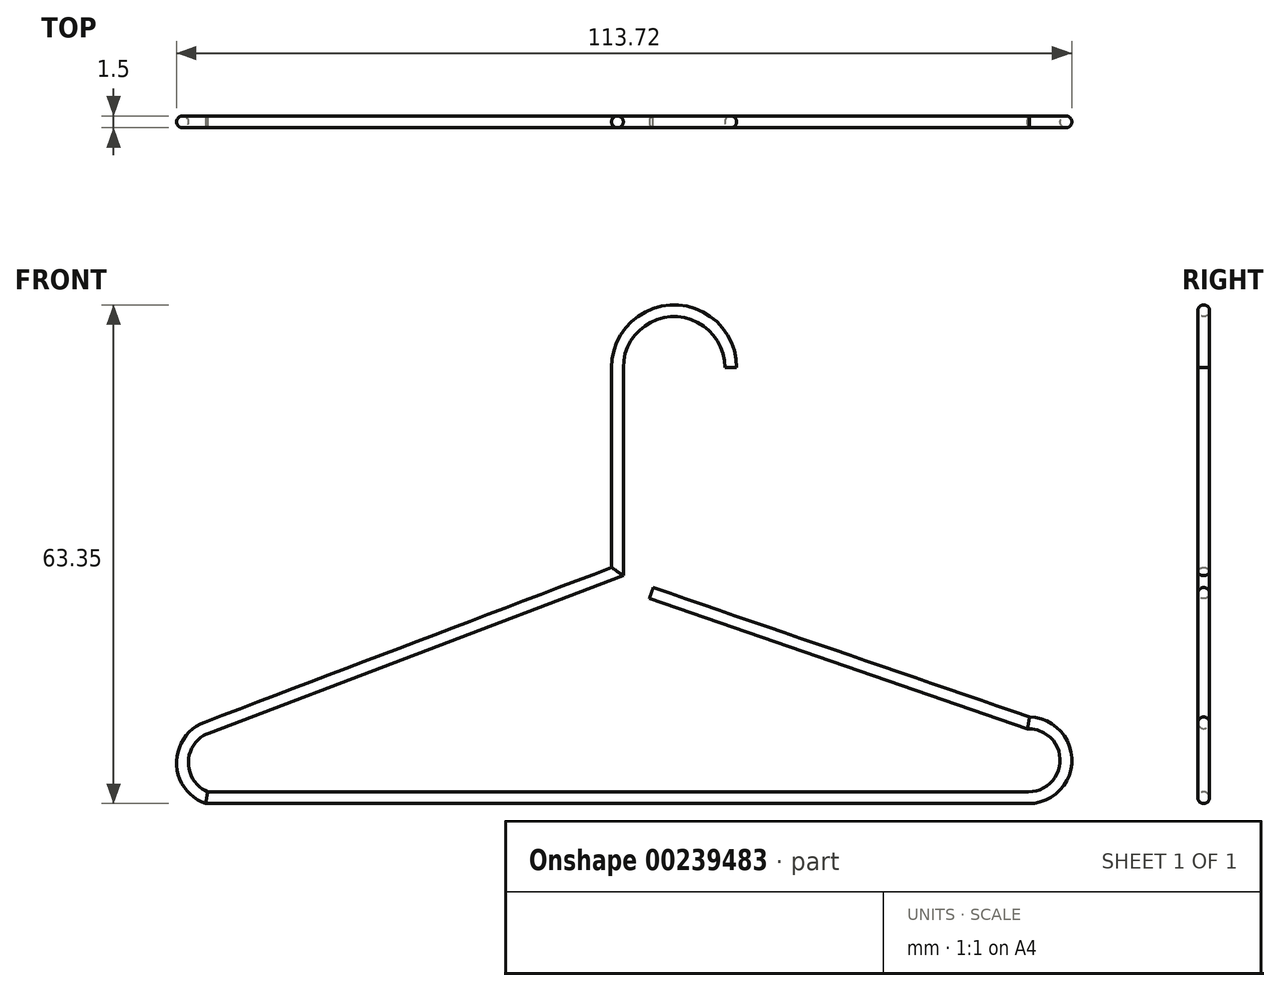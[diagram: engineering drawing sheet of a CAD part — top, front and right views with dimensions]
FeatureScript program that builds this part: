
annotation { "Feature Type Name" : "Feature", "Feature Type Description" : "" }
export const myFeature = defineFeature(function(context is Context, id is Id, definition is map)
    precondition{}
    {
        {
            var Q0;
            Q0=qCreatedBy(makeId("Front.planeOp"),FACE);
            var sketch = newSketch(context, id + "F0", { "sketchPlane" : qUnion([Q0])});
            skLineSegment(sketch, "E0", {"start": v(0, 0) * mm, "end": v(0, 25.95) * mm});
            skArc(sketch, "E1", {"start": v(14.35, 25.95) * mm, "mid": v(7.17, 33.12) * mm, "end": v(0, 25.95) * mm});
            skLineSegment(sketch, "E2", {"start": v(0, 0) * mm, "end": v(-52.2, -19.84) * mm});
            skArc(sketch, "E3", {"start": v(-52.2, -19.84) * mm, "mid": v(-55.25, -24.27) * mm, "end": v(-52.2, -28.7) * mm});
            skLineSegment(sketch, "E4", {"start": v(-52.2, -28.7) * mm, "end": v(52.2, -28.7) * mm});
            skArc(sketch, "E5", {"start": v(52.2, -28.7) * mm, "mid": v(56.94, -23.96) * mm, "end": v(52.2, -19.22) * mm});
            skLineSegment(sketch, "E6", {"start": v(52.2, -19.22) * mm, "end": v(4.27, -2.75) * mm});
            skSolve(sketch);
        }
        {
            var Q0;
            Q0=sQuery(id+"F0.wireOp",VERTEX,"E1.start");
            var Q1;
            Q1=qCreatedBy(makeId("Top.planeOp"),FACE);
            cPlane(context, id + "F1", {"entities" : qUnion([Q0, Q1]), "cplaneType" : CPlaneType.PLANE_POINT, "offset" : 25.4 * mm, "width" : 152.4 * mm, "height" : 152.4 * mm});
        }
        {
            var Q0;
            Q0=qCreatedBy(id+"F1.planeOp",FACE);
            var sketch = newSketch(context, id + "F2", { "sketchPlane" : qUnion([Q0])});
            skCircle(sketch, "E7", {"center": v(14.37, 0) * mm, "radius": 0.75 * mm});
            skSolve(sketch);
        }
        {
            var Q0;
            Q0 = qSketchRegion(id + "F2", true);
            var Q1;
            Q1 = qConstructionFilter(qBodyType(qCreatedBy(id + "F0" ,EDGE), BodyType.WIRE), ConstructionObject.NO);
            sweep(context, id + "F3", {"profiles" : qUnion([Q0]), "path" : qUnion([Q1])});
        }
    });
